# Revit family: Haworth_Intuity_Benching_BenchEnd
name_source: partatom
category: Furniture Systems
revit_build: Autodesk Revit 2018 (Build: 20170223_1515(x64)
units: mm (PartAtom-declared; Revit-internal decimal feet)

## family parameters
Always vertical = Yes
Cut with Voids When Loaded = No
OmniClass Number = 23.40.70.14.64.21
OmniClass Title = Systems Furniture
Part Type = Normal
Room Calculation Point = No
Round Connector Dimension = Use Diameter
Shared = No
Work Plane-Based = No

## types (8) — shared parameters
Actual Height = 29 3/16"
Assembly Code = E2020200
Custom Size = Yes
Description = Haworth - Intuity Benching - Bench End
Leg Height = 28"
Leg Offset Depth = 3 1/2"
Leg Offset Width = 4 1/2"
Manufacturer = Haworth
Max Width = 30"
Min Width = 24"
Model = Haworth Intuity
Revision Number = 4
Size = Verify Final Dim. w/ Haworth
Standard Depths = 51, 63 inches
Standard Widths = 24, 30 inches
Sustainability Info = https://www.haworth.com
Top Thickness = 1 3/16"
URL = www.haworth.com
URL - Product = http://www.haworth.com
Warranty = http://www.haworth.com

## per-type parameters (varying)
| type | 51 Depth | 63 Depth | Actual Width | Actual Worksurface Depth | Angled Leg | Straight Leg | Width |
| 51d 24w - Straight Leg | Yes | No | 24" | 50 13/16" | No | Yes | 24" |
| 51d 30w - Straight Leg | Yes | No | 30" | 50 13/16" | No | Yes | 30" |
| 63d 24w - Straight Leg | No | Yes | 24" | 62 13/16" | No | Yes | 24" |
| 63d 30w - Straight Leg | No | Yes | 30" | 62 13/16" | No | Yes | 30" |
| 63d 30w - Angled Leg | No | Yes | 30" | 62 13/16" | Yes | No | 30" |
| 63d 24w - Angled Leg | No | Yes | 24" | 62 13/16" | Yes | No | 24" |
| 51d 30w - Angled Leg | Yes | No | 30" | 50 13/16" | Yes | No | 30" |
| 51d 24w - Angled Leg | Yes | No | 24" | 50 13/16" | Yes | No | 24" |

## geometry (parser evidence)
native form markers: Sweep x8
no freeform markers — native parametric forms only
